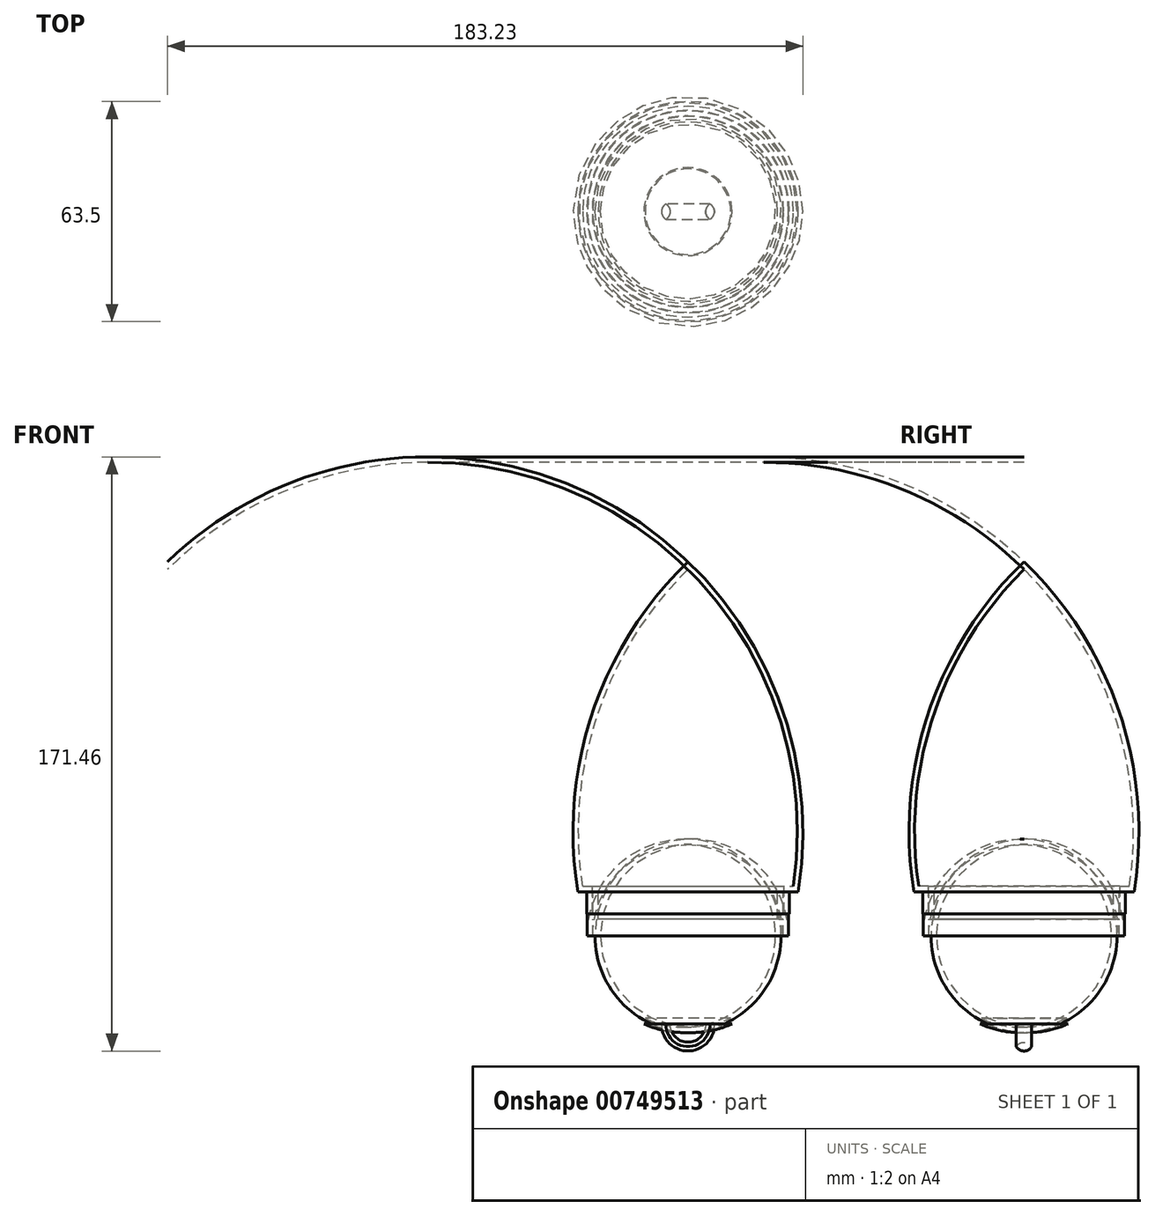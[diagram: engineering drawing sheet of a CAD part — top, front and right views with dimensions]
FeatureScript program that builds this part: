
annotation { "Feature Type Name" : "Feature", "Feature Type Description" : "" }
export const myFeature = defineFeature(function(context is Context, id is Id, definition is map)
    precondition{}
    {
        {
            var Q0;
            Q0=qCreatedBy(makeId("Front.planeOp"),FACE);
            var sketch = newSketch(context, id + "F0", { "sketchPlane" : qUnion([Q0])});
            skLineSegment(sketch, "E0", {"start": v(0, 0) * mm, "end": v(-29.21, 0) * mm});
            skLineSegment(sketch, "E1", {"start": v(-29.21, 0) * mm, "end": v(-29.21, 6.35) * mm});
            skLineSegment(sketch, "E2", {"start": v(-29.21, 6.35) * mm, "end": v(-31.75, 6.35) * mm});
            skLineSegment(sketch, "E3", {"start": v(0, 0) * mm, "end": v(0, 101.6) * mm});
            skArc(sketch, "E4", {"start": v(0, 101.6) * mm, "mid": v(-27.6, 57.88) * mm, "end": v(-31.75, 6.35) * mm});
            skArc(sketch, "E5.0", {"start": v(3.9, 103.05) * mm, "mid": v(-25.24, 59.82) * mm, "end": v(-30.4, 7.94) * mm});
            skLineSegment(sketch, "E5.1", {"start": v(-27.62, 7.94) * mm, "end": v(-30.4, 7.94) * mm});
            skLineSegment(sketch, "E5.2", {"start": v(-27.62, 0) * mm, "end": v(-27.62, 7.94) * mm});
            skLineSegment(sketch, "E6.MirrorCS", {"start": v(-30.85, 6.35) * mm, "end": v(-30.85, 6.26) * mm});
            skLineSegment(sketch, "E7.MirrorCS", {"start": v(-29.21, 0.06) * mm, "end": v(-29.27, 0.06) * mm});
            skPoint(sketch, "E8.start.orphan", {"position": v(107.91, -6.25) * mm});
            skPoint(sketch, "E9.start.orphan", {"position": v(107.91, -12.6) * mm});
            skPoint(sketch, "E10.end.orphan", {"position": v(109.5, -18.95) * mm});
            skPoint(sketch, "E10.start.orphan", {"position": v(109.5, -12.6) * mm});
            skPoint(sketch, "E11.end.orphan", {"position": v(89.76, -44.35) * mm});
            skPoint(sketch, "E12.MirrorCS.end.orphan", {"position": v(-30.85, 6.35) * mm});
            skPoint(sketch, "E12.MirrorCS.start.orphan", {"position": v(0, 6.35) * mm});
            skLineSegment(sketch, "E13", {"start": v(0, 6.35) * mm, "end": v(27.43, 6.35) * mm});
            skLineSegment(sketch, "E14", {"start": v(27.43, 6.35) * mm, "end": v(27.43, 0) * mm});
            skLineSegment(sketch, "E15", {"start": v(27.43, 0) * mm, "end": v(29.02, 0) * mm});
            skLineSegment(sketch, "E16", {"start": v(29.02, 0) * mm, "end": v(29.02, -6.35) * mm});
            skLineSegment(sketch, "E17", {"start": v(0, 6.35) * mm, "end": v(0, -31.75) * mm});
            skLineSegment(sketch, "E18", {"start": v(0, -31.75) * mm, "end": v(12.7, -31.75) * mm});
            skArc(sketch, "E19", {"start": v(12.7, -31.75) * mm, "mid": v(24.59, -21.45) * mm, "end": v(29.02, -6.35) * mm});
            skLineSegment(sketch, "E20.0", {"start": v(0, -30.16) * mm, "end": v(12.35, -30.16) * mm});
            skLineSegment(sketch, "E20.1", {"start": v(25.84, 6.35) * mm, "end": v(25.84, -1.59) * mm});
            skLineSegment(sketch, "E20.2", {"start": v(25.84, -1.59) * mm, "end": v(27.43, -1.59) * mm});
            skLineSegment(sketch, "E20.3", {"start": v(27.43, -1.59) * mm, "end": v(27.43, -6.35) * mm});
            skArc(sketch, "E20.4", {"start": v(12.35, -30.16) * mm, "mid": v(23.34, -20.44) * mm, "end": v(27.43, -6.35) * mm});
            skSolve(sketch);
        }
        {
            var Q0;
            {var subQ4=sQuery(id+"F0.wireOp",EDGE,"E1");Q0=makeQuery(id+"F0.imprint","IMPRINT",FACE,{"disambiguationData":[TD([[makeQuery(id+"F0.imprint","IMPRINT",EDGE,{"derivedFrom":subQ4}),-1.0]])]});}
            var Q1;
            Q1=sQuery(id+"F0.wireOp",EDGE,"E3");
            revolve(context, id + "F1", {"surfaceOperationType" : NewSurfaceOperationType.NEW, "entities" : qUnion([Q0]), "axis" : qUnion([Q1]), "revolveType" : RevolveType.FULL});
        }
        {
            var Q0;
            {var subQ4=sQuery(id+"F0.wireOp",EDGE,"E14");Q0=makeQuery(id+"F0.imprint","IMPRINT",FACE,{"disambiguationData":[TD([[makeQuery(id+"F0.imprint","IMPRINT",EDGE,{"derivedFrom":subQ4}),-1.0]])]});}
            var Q1;
            Q1=sQuery(id+"F0.wireOp",EDGE,"E17");
            revolve(context, id + "F2", {"surfaceOperationType" : NewSurfaceOperationType.NEW, "entities" : qUnion([Q0]), "axis" : qUnion([Q1]), "revolveType" : RevolveType.FULL});
        }
        {
            var Q0;
            Q0=qCreatedBy(makeId("Front.planeOp"),FACE);
            var sketch = newSketch(context, id + "F3", { "sketchPlane" : qUnion([Q0])});
            skCircle(sketch, "E21", {"center": v(0, -31.75) * mm, "radius": 0.97 * mm});
            skLineSegment(sketch, "E22", {"start": v(0, -31.75) * mm, "end": v(-7.62, -31.75) * mm});
            skLineSegment(sketch, "E23", {"start": v(0, -31.75) * mm, "end": v(7.62, -31.75) * mm});
            skArc(sketch, "E24", {"start": v(-7.62, -31.75) * mm, "mid": v(0, -39.6) * mm, "end": v(7.62, -31.75) * mm});
            skLineSegment(sketch, "E25", {"start": v(0, -31.75) * mm, "end": v(-5.08, -31.75) * mm});
            skLineSegment(sketch, "E26", {"start": v(0, -31.75) * mm, "end": v(5.08, -31.75) * mm});
            skArc(sketch, "E27", {"start": v(-5.08, -31.75) * mm, "mid": v(0, -37.05) * mm, "end": v(5.08, -31.75) * mm});
            skSolve(sketch);
        }
        {
            var Q0;
            {var subQ0=sQuery(id+"F3.wireOp",EDGE,"E24");Q0=makeQuery(id+"F3.imprint","IMPRINT",FACE,{"disambiguationData":[TD([[makeQuery(id+"F3.imprint","IMPRINT",EDGE,{"derivedFrom":subQ0}),1.0]])]});}
            extrude(context, id + "F4", {"entities" : qUnion([Q0]), "operationType" : NewBodyOperationType.ADD, "endBound" : BoundingType.SYMMETRIC, "depth" : 5.08 * mm, "offsetDistance" : 25.4 * mm});
        }
        {
            var Q0;
            Q0=makeQuery(id+"F4.opExtrude","CAP_EDGE",EDGE,{"disambiguationData":[OSD([sQuery(id+"F3.wireOp",EDGE,"E24")])],"isStart":false});
            var Q1;
            Q1=makeQuery(id+"F4.opExtrude","CAP_EDGE",EDGE,{"disambiguationData":[OSD([sQuery(id+"F3.wireOp",EDGE,"E24")])],"isStart":true});
            var Q2;
            Q2=makeQuery(id+"F4.opExtrude","CAP_EDGE",EDGE,{"disambiguationData":[OSD([sQuery(id+"F3.wireOp",EDGE,"E27")])],"isStart":false});
            var Q3;
            Q3=makeQuery(id+"F4.opExtrude","CAP_EDGE",EDGE,{"disambiguationData":[OSD([sQuery(id+"F3.wireOp",EDGE,"E27")])],"isStart":true});
            fillet(context, id + "F5", {"entities" : qUnion([Q0, Q1, Q2, Q3]), "radius" : 2.54 * mm, "tangentPropagation" : true, "allowEdgeOverflow" : false});
        }
    });
